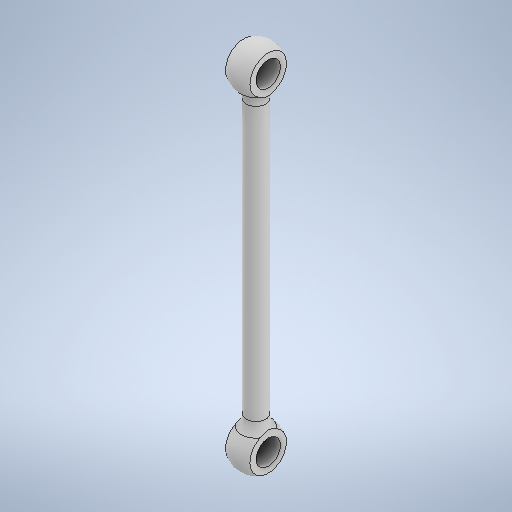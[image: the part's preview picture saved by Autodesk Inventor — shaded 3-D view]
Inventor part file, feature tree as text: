
AUTODESK INVENTOR PART (.ipt)
format: ipt  version: 2025.1 (Build 291241000, 241)  size: 303,616 bytes
history: native  units: mm
features: sketch x3, plane x2, revolve x1, extrude x1, hole x1, mirror x1
ambient origin geometry x8: Origin, YZ Plane, XZ Plane, XY Plane, X Axis, Y Axis, Z Axis, Center Point
bodies: Volumenkörper1 (feature_tree)
feature tree (9):
  revolve  "Umdrehung1"
  plane  "Arbeitsebene1"
  extrude  "Extrusion1"  Depth=4.5mm
  hole  "Bohrung1"  [1 undecoded]
  plane  "Arbeitsebene2"
  mirror  "Spiegeln1"
  sketch  "Skizze1"  dims[d0=4.5mm d1=4.0mm]
  sketch  "Skizze2"  dims[d2=58.0mm d3=3.0mm]
  sketch  "Skizze3"  dims[d4=90.0deg d5=-62.5mm d6=5.0mm d7=9.0mm d8=0.0mm d9=5.0mm d10=6.0mm d11=4.0mm d12=2.0mm d13=90.0deg d14=8.0mm d15=20.594885mm d16=-24.5mm]
note: 1 required parameter value undecoded (feature->parameter linkage not recoverable at this tier; creation-order binding heuristic only, values carry confidence <= 0.55)
